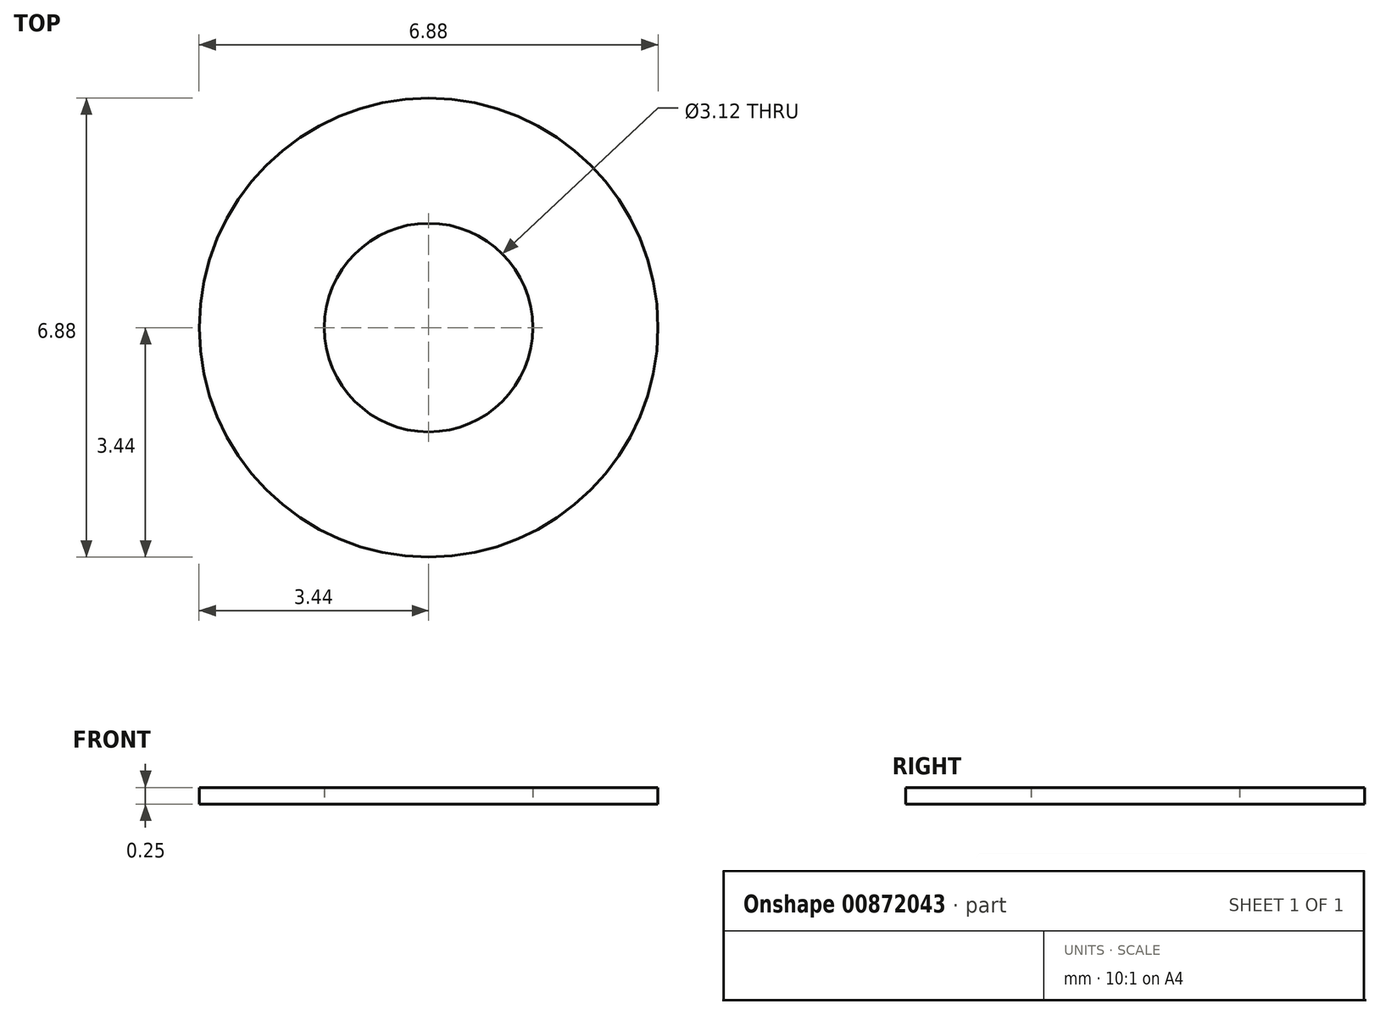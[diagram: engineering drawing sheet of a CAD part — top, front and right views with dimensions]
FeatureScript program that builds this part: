
annotation { "Feature Type Name" : "Feature", "Feature Type Description" : "" }
export const myFeature = defineFeature(function(context is Context, id is Id, definition is map)
    precondition{}
    {
        {
            var Q0;
            Q0=qCreatedBy(makeId("Top.planeOp"),FACE);
            var sketch = newSketch(context, id + "F0", { "sketchPlane" : qUnion([Q0])});
            skCircle(sketch, "E0", {"center": v(0, 0) * mm, "radius": 1.56 * mm});
            skCircle(sketch, "E1", {"center": v(0, 0) * mm, "radius": 3.44 * mm});
            skSolve(sketch);
        }
        {
            var Q0;
            Q0=makeQuery(id+"F0.imprint","IMPRINT",FACE,{"disambiguationData":[TD([[makeQuery(id+"F0.imprint","IMPRINT",EDGE,{"derivedFrom":sQuery(id+"F0.wireOp",EDGE,"E0")}),-1.0]])]});
            extrude(context, id + "F1", {"entities" : qUnion([Q0]), "depth" : .25 * mm, "offsetDistance" : 25 * mm});
        }
    });
